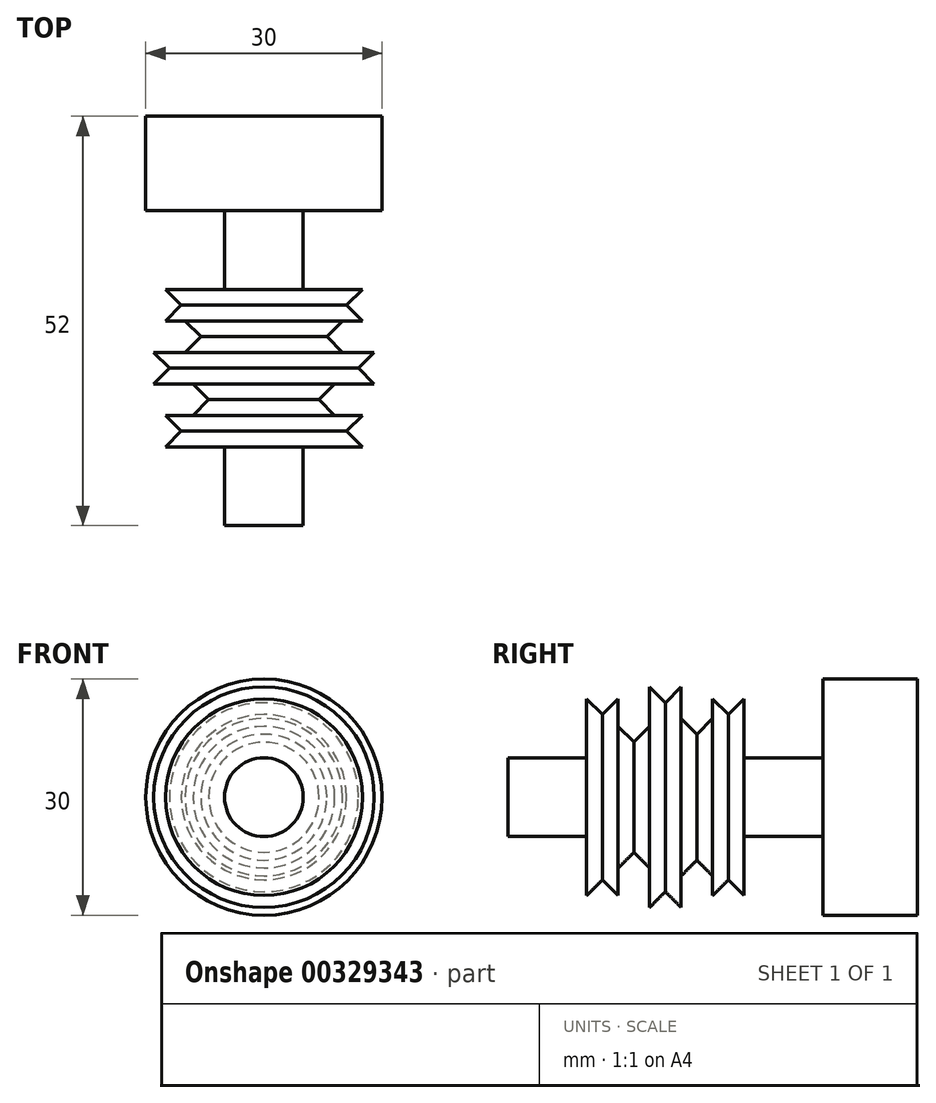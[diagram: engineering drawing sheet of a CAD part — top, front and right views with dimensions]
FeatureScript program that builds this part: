
annotation { "Feature Type Name" : "Feature", "Feature Type Description" : "" }
export const myFeature = defineFeature(function(context is Context, id is Id, definition is map)
    precondition{}
    {
        {
            var Q0;
            Q0=qCreatedBy(makeId("Front.planeOp"),FACE);
            var sketch = newSketch(context, id + "F0", { "sketchPlane" : qUnion([Q0])});
            skCircle(sketch, "E0", {"center": v(0, 0) * mm, "radius": 15 * mm});
            skSolve(sketch);
        }
        {
            var Q0;
            Q0=makeQuery(id+"F0.imprint","IMPRINT",FACE,{"disambiguationData":[TD([[makeQuery(id+"F0.imprint","IMPRINT",EDGE,{"derivedFrom":sQuery(id+"F0.wireOp",EDGE,"E0")}),1.0]])]});
            var Q1;
            Q1=sQuery(id+"F0.wireOp",EDGE,"E0");
            extrude(context, id + "F1", {"entities" : qUnion([Q0]), "surfaceEntities" : qUnion([Q1]), "depth" : 12 * mm});
        }
        {
            var Q0;
            Q0=makeQuery(id+"F1.opExtrude","CAP_FACE",FACE,{"disambiguationData":[OSD([sQuery(id+"F0.wireOp",EDGE,"E0")])],"isStart":false});
            var sketch = newSketch(context, id + "F2", { "sketchPlane" : qUnion([Q0])});
            skCircle(sketch, "E1", {"center": v(0, 0) * mm, "radius": 5 * mm});
            skSolve(sketch);
        }
        {
            var Q0;
            Q0 = qSketchRegion(id + "F2", true);
            extrude(context, id + "F3", {"entities" : qUnion([Q0]), "operationType" : NewBodyOperationType.ADD, "depth" : 10 * mm});
        }
        {
            var Q0;
            Q0=makeQuery(id+"F3.opExtrude","CAP_FACE",FACE,{"disambiguationData":[OSD([sQuery(id+"F2.wireOp",EDGE,"E1")])],"isStart":false});
            var sketch = newSketch(context, id + "F4", { "sketchPlane" : qUnion([Q0])});
            skCircle(sketch, "E2", {"center": v(0, 0) * mm, "radius": 12.5 * mm});
            skSolve(sketch);
        }
        {
            var Q0;
            Q0 = qSketchRegion(id + "F4", true);
            extrude(context, id + "F5", {"entities" : qUnion([Q0]), "operationType" : NewBodyOperationType.ADD, "depth" : 2 * mm, "hasDraft" : true, "draftAngle" : 45 * degree, "draftPullDirection" : true});
        }
        {
            var Q0;
            Q0=makeQuery(id+"F5.opExtrude","CAP_FACE",FACE,{"disambiguationData":[OSD([sQuery(id+"F4.wireOp",EDGE,"E2")])],"isStart":false});
            var sketch = newSketch(context, id + "F6", { "sketchPlane" : qUnion([Q0])});
            skCircle(sketch, "E3.0", {"center": v(0, 0) * mm, "radius": 10.5 * mm});
            skSolve(sketch);
        }
        {
            var Q0;
            Q0 = qSketchRegion(id + "F6", true);
            extrude(context, id + "F7", {"entities" : qUnion([Q0]), "operationType" : NewBodyOperationType.ADD, "depth" : 2 * mm, "hasDraft" : true, "draftAngle" : 45 * degree});
        }
        {
            var Q0;
            Q0=makeQuery(id+"F7.opExtrude","CAP_FACE",FACE,{"disambiguationData":[OSD([sQuery(id+"F6.wireOp",EDGE,"E3.0")])],"isStart":false});
            var sketch = newSketch(context, id + "F8", { "sketchPlane" : qUnion([Q0])});
            skCircle(sketch, "E4", {"center": v(0, 0) * mm, "radius": 10 * mm});
            skSolve(sketch);
        }
        {
            var Q0;
            Q0=makeQuery(id+"F8.imprint","IMPRINT",FACE,{"disambiguationData":[TD([[makeQuery(id+"F8.imprint","IMPRINT",EDGE,{"derivedFrom":sQuery(id+"F8.wireOp",EDGE,"E4")}),1.0]])]});
            var Q1;
            Q1=sQuery(id+"F8.wireOp",EDGE,"E4");
            extrude(context, id + "F9", {"entities" : qUnion([Q0]), "operationType" : NewBodyOperationType.ADD, "surfaceEntities" : qUnion([Q1]), "depth" : 2 * mm, "hasDraft" : true, "draftAngle" : 45 * degree, "draftPullDirection" : true});
        }
        {
            var Q0;
            Q0=makeQuery(id+"F9.opExtrude","CAP_FACE",FACE,{"disambiguationData":[OSD([sQuery(id+"F8.wireOp",EDGE,"E4")])],"isStart":false});
            var sketch = newSketch(context, id + "F10", { "sketchPlane" : qUnion([Q0])});
            skCircle(sketch, "E5.0", {"center": v(0, 0) * mm, "radius": 8 * mm});
            skSolve(sketch);
        }
        {
            var Q0;
            Q0 = qSketchRegion(id + "F10", true);
            extrude(context, id + "F11", {"entities" : qUnion([Q0]), "operationType" : NewBodyOperationType.ADD, "depth" : 2 * mm, "hasDraft" : true, "draftAngle" : 45 * degree});
        }
        {
            var Q0;
            Q0=makeQuery(id+"F11.opExtrude","CAP_FACE",FACE,{"disambiguationData":[OSD([sQuery(id+"F10.wireOp",EDGE,"E5.0")])],"isStart":false});
            var sketch = newSketch(context, id + "F12", { "sketchPlane" : qUnion([Q0])});
            skCircle(sketch, "E6", {"center": v(0, 0) * mm, "radius": 14 * mm});
            skSolve(sketch);
        }
        {
            var Q0;
            Q0 = qSketchRegion(id + "F12", true);
            extrude(context, id + "F13", {"entities" : qUnion([Q0]), "operationType" : NewBodyOperationType.ADD, "depth" : 2 * mm, "hasDraft" : true, "draftAngle" : 45 * degree, "draftPullDirection" : true});
        }
        {
            var Q0;
            Q0=makeQuery(id+"F13.opExtrude","CAP_FACE",FACE,{"disambiguationData":[OSD([sQuery(id+"F12.wireOp",EDGE,"E6")])],"isStart":false});
            var sketch = newSketch(context, id + "F14", { "sketchPlane" : qUnion([Q0])});
            skCircle(sketch, "E7.0", {"center": v(0, 0) * mm, "radius": 12 * mm});
            skSolve(sketch);
        }
        {
            var Q0;
            Q0 = qSketchRegion(id + "F14", true);
            extrude(context, id + "F15", {"entities" : qUnion([Q0]), "operationType" : NewBodyOperationType.ADD, "depth" : 2 * mm, "hasDraft" : true, "draftAngle" : 45 * degree});
        }
        {
            var Q0;
            Q0=makeQuery(id+"F15.opExtrude","CAP_FACE",FACE,{"disambiguationData":[OSD([sQuery(id+"F14.wireOp",EDGE,"E7.0")])],"isStart":false});
            var sketch = newSketch(context, id + "F16", { "sketchPlane" : qUnion([Q0])});
            skCircle(sketch, "E8", {"center": v(0, 0) * mm, "radius": 9 * mm});
            skSolve(sketch);
        }
        {
            var Q0;
            Q0 = qSketchRegion(id + "F16", true);
            extrude(context, id + "F17", {"entities" : qUnion([Q0]), "operationType" : NewBodyOperationType.ADD, "depth" : 2 * mm, "hasDraft" : true, "draftAngle" : 45 * degree, "draftPullDirection" : true});
        }
        {
            var Q0;
            Q0=makeQuery(id+"F17.opExtrude","CAP_FACE",FACE,{"disambiguationData":[OSD([sQuery(id+"F16.wireOp",EDGE,"E8")])],"isStart":false});
            var sketch = newSketch(context, id + "F18", { "sketchPlane" : qUnion([Q0])});
            skCircle(sketch, "E9.0", {"center": v(0, 0) * mm, "radius": 7 * mm});
            skSolve(sketch);
        }
        {
            var Q0;
            Q0 = qSketchRegion(id + "F18", true);
            extrude(context, id + "F19", {"entities" : qUnion([Q0]), "operationType" : NewBodyOperationType.ADD, "depth" : 2 * mm, "hasDraft" : true, "draftAngle" : 45 * degree});
        }
        {
            var Q0;
            Q0=makeQuery(id+"F19.opExtrude","CAP_FACE",FACE,{"disambiguationData":[OSD([sQuery(id+"F18.wireOp",EDGE,"E9.0")])],"isStart":false});
            var sketch = newSketch(context, id + "F20", { "sketchPlane" : qUnion([Q0])});
            skCircle(sketch, "E10", {"center": v(0, 0) * mm, "radius": 12.5 * mm});
            skSolve(sketch);
        }
        {
            var Q0;
            Q0 = qSketchRegion(id + "F20", true);
            extrude(context, id + "F21", {"entities" : qUnion([Q0]), "operationType" : NewBodyOperationType.ADD, "depth" : 2 * mm, "hasDraft" : true, "draftAngle" : 45 * degree, "draftPullDirection" : true});
        }
        {
            var Q0;
            Q0=makeQuery(id+"F21.opExtrude","CAP_FACE",FACE,{"disambiguationData":[OSD([sQuery(id+"F20.wireOp",EDGE,"E10")])],"isStart":false});
            var sketch = newSketch(context, id + "F22", { "sketchPlane" : qUnion([Q0])});
            skCircle(sketch, "E11.0", {"center": v(0, 0) * mm, "radius": 10.5 * mm});
            skSolve(sketch);
        }
        {
            var Q0;
            Q0 = qSketchRegion(id + "F22", true);
            extrude(context, id + "F23", {"entities" : qUnion([Q0]), "operationType" : NewBodyOperationType.ADD, "depth" : 2 * mm, "hasDraft" : true, "draftAngle" : 45 * degree});
        }
        {
            var Q0;
            Q0=makeQuery(id+"F23.opExtrude","CAP_FACE",FACE,{"disambiguationData":[OSD([sQuery(id+"F22.wireOp",EDGE,"E11.0")])],"isStart":false});
            var sketch = newSketch(context, id + "F24", { "sketchPlane" : qUnion([Q0])});
            skCircle(sketch, "E12", {"center": v(0, 0) * mm, "radius": 5 * mm});
            skSolve(sketch);
        }
        {
            var Q0;
            Q0 = qSketchRegion(id + "F24", true);
            extrude(context, id + "F25", {"entities" : qUnion([Q0]), "operationType" : NewBodyOperationType.ADD, "depth" : 10 * mm});
        }
    });
